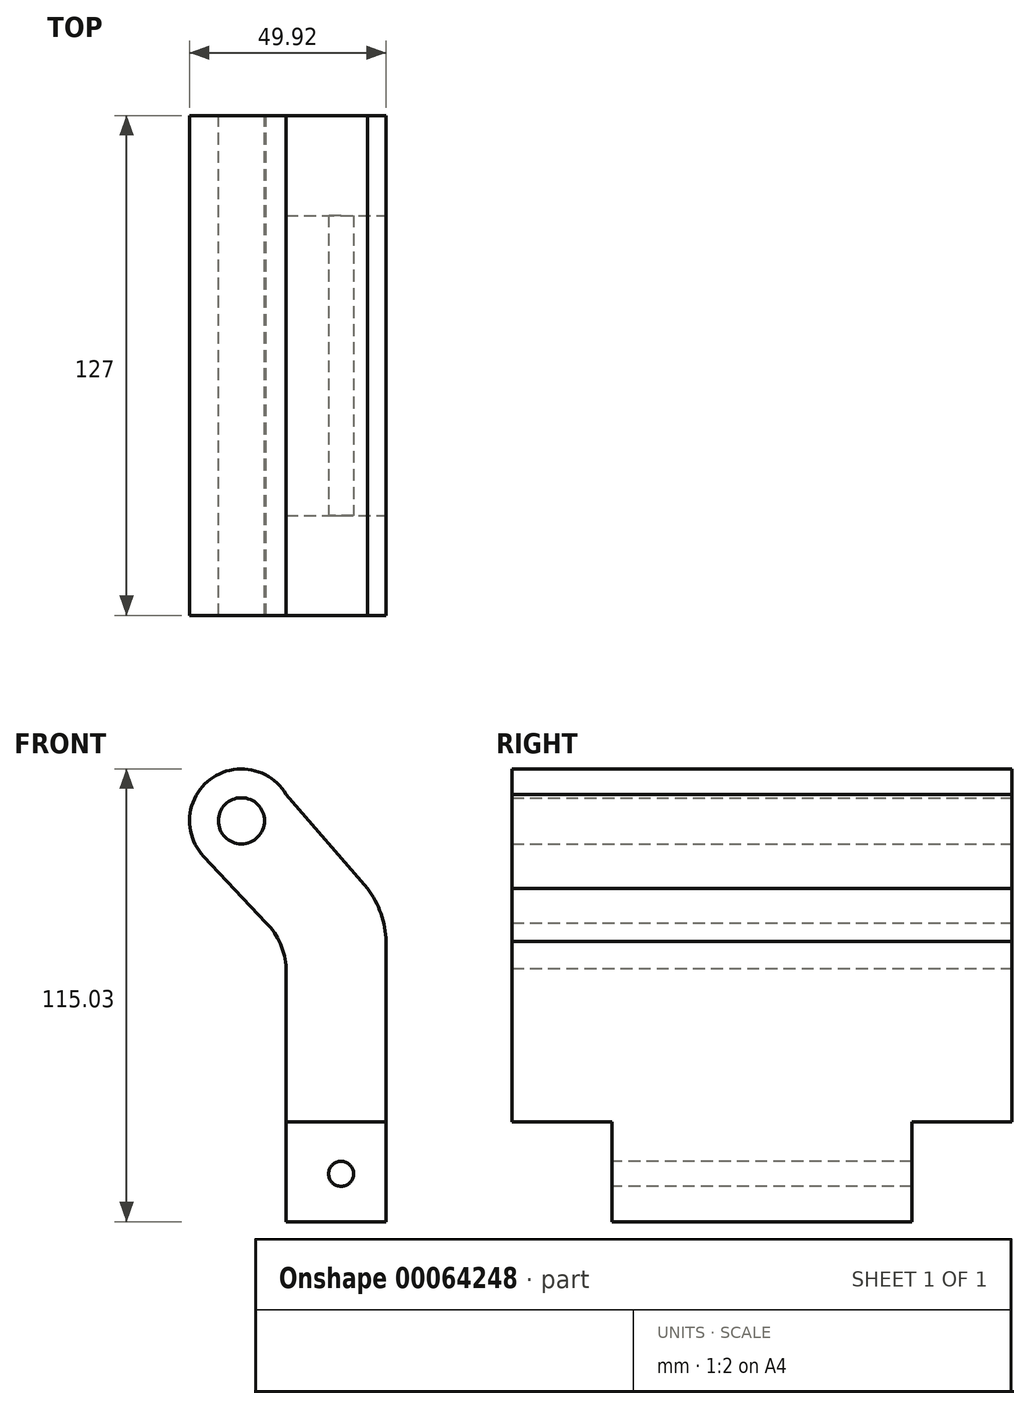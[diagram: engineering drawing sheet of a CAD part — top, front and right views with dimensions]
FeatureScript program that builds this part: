
annotation { "Feature Type Name" : "Feature", "Feature Type Description" : "" }
export const myFeature = defineFeature(function(context is Context, id is Id, definition is map)
    precondition{}
    {
        {
            var Q0;
            Q0=qCreatedBy(makeId("Front.planeOp"),FACE);
            var sketch = newSketch(context, id + "F0", { "sketchPlane" : qUnion([Q0])});
            skLineSegment(sketch, "E0", {"start": v(-13.98, -40.84) * mm, "end": v(11.42, -40.84) * mm});
            skLineSegment(sketch, "E1", {"start": v(-13.98, -40.84) * mm, "end": v(-13.98, 23.48) * mm});
            skLineSegment(sketch, "E2", {"start": v(-18.39, 34.43) * mm, "end": v(-34.91, 51.97) * mm});
            skLineSegment(sketch, "E3", {"start": v(11.42, -40.84) * mm, "end": v(11.42, 30.32) * mm});
            skLineSegment(sketch, "E4", {"start": v(6.68, 43.76) * mm, "end": v(-13.98, 67.73) * mm});
            skArc(sketch, "E5", {"start": v(-13.98, 67.73) * mm, "mid": v(-33.24, 71.54) * mm, "end": v(-34.91, 51.97) * mm});
            skArc(sketch, "E6", {"start": v(-13.98, 23.48) * mm, "mid": v(-15.4, 29.75) * mm, "end": v(-19, 35.08) * mm});
            skArc(sketch, "E7", {"start": v(11.42, 29.42) * mm, "mid": v(10.28, 37) * mm, "end": v(6.68, 43.76) * mm});
            skCircle(sketch, "E8", {"center": v(-25.32, 61) * mm, "radius": 5.86 * mm});
            skSolve(sketch);
        }
        {
            var Q0;
            {var subQ1=sQuery(id+"F0.wireOp",EDGE,"E0");Q0=makeQuery(id+"F0.imprint","IMPRINT",FACE,{"disambiguationData":[TD([[makeQuery(id+"F0.imprint","IMPRINT",EDGE,{"derivedFrom":subQ1}),1.0]])]});}
            extrude(context, id + "F1", {"entities" : qUnion([Q0]), "depth" : 127 * mm});
        }
        {
            var Q0;
            Q0=makeQuery(id+"F1.opExtrude","CAP_FACE",FACE,{"disambiguationData":[OSD([sQuery(id+"F0.wireOp",EDGE,"E0"),sQuery(id+"F0.wireOp",EDGE,"E1"),sQuery(id+"F0.wireOp",EDGE,"E2"),sQuery(id+"F0.wireOp",EDGE,"E3"),sQuery(id+"F0.wireOp",EDGE,"E4"),sQuery(id+"F0.wireOp",EDGE,"E5"),sQuery(id+"F0.wireOp",EDGE,"E6"),sQuery(id+"F0.wireOp",EDGE,"E7")])],"isStart":false});
            var sketch = newSketch(context, id + "F2", { "sketchPlane" : qUnion([Q0])});
            skLineSegment(sketch, "E9", {"start": v(-13.98, -15.44) * mm, "end": v(11.42, -15.44) * mm});
            skLineSegment(sketch, "E10", {"start": v(11.42, -15.44) * mm, "end": v(11.42, -40.84) * mm});
            skLineSegment(sketch, "E11", {"start": v(11.42, -40.84) * mm, "end": v(-13.98, -40.84) * mm});
            skLineSegment(sketch, "E12", {"start": v(-13.98, -40.84) * mm, "end": v(-13.98, -15.44) * mm});
            skSolve(sketch);
        }
        {
            var Q0;
            Q0=makeQuery(id+"F2.imprint","IMPRINT",FACE,{"disambiguationData":[TD([[makeQuery(id+"F2.imprint","IMPRINT",EDGE,{"derivedFrom":sQuery(id+"F2.wireOp",EDGE,"E9")}),-1.0]])]});
            extrude(context, id + "F3", {"entities" : qUnion([Q0]), "operationType" : NewBodyOperationType.REMOVE, "oppositeDirection" : true, "depth" : 25.4 * mm});
        }
        {
            var Q0;
            Q0=makeQuery(id+"F1.opExtrude","CAP_FACE",FACE,{"disambiguationData":[OSD([sQuery(id+"F0.wireOp",EDGE,"E0"),sQuery(id+"F0.wireOp",EDGE,"E1"),sQuery(id+"F0.wireOp",EDGE,"E2"),sQuery(id+"F0.wireOp",EDGE,"E3"),sQuery(id+"F0.wireOp",EDGE,"E4"),sQuery(id+"F0.wireOp",EDGE,"E5"),sQuery(id+"F0.wireOp",EDGE,"E6"),sQuery(id+"F0.wireOp",EDGE,"E7")])],"isStart":true});
            var sketch = newSketch(context, id + "F4", { "sketchPlane" : qUnion([Q0])});
            skLineSegment(sketch, "E13", {"start": v(-11.42, -15.44) * mm, "end": v(13.98, -15.44) * mm});
            skLineSegment(sketch, "E14", {"start": v(13.98, -15.44) * mm, "end": v(13.98, -40.84) * mm});
            skLineSegment(sketch, "E15", {"start": v(13.98, -40.84) * mm, "end": v(-11.42, -40.84) * mm});
            skLineSegment(sketch, "E16", {"start": v(-11.42, -40.84) * mm, "end": v(-11.42, -15.44) * mm});
            skSolve(sketch);
        }
        {
            var Q0;
            Q0=makeQuery(id+"F4.imprint","IMPRINT",FACE,{"disambiguationData":[TD([[makeQuery(id+"F4.imprint","IMPRINT",EDGE,{"derivedFrom":sQuery(id+"F4.wireOp",EDGE,"E13")}),-1.0]])]});
            extrude(context, id + "F5", {"entities" : qUnion([Q0]), "operationType" : NewBodyOperationType.REMOVE, "oppositeDirection" : true, "depth" : 25.4 * mm});
        }
        {
            var Q0;
            Q0=makeQuery(id+"F3.boolean.opBoolean","COPY",FACE,{"derivedFrom":makeQuery(id+"F3.opExtrude","CAP_FACE",FACE,{"disambiguationData":[OSD([sQuery(id+"F2.wireOp",EDGE,"E9"),sQuery(id+"F2.wireOp",EDGE,"E10"),sQuery(id+"F2.wireOp",EDGE,"E11"),sQuery(id+"F2.wireOp",EDGE,"E12")])],"isStart":false})});
            var sketch = newSketch(context, id + "F6", { "sketchPlane" : qUnion([Q0])});
            skCircle(sketch, "E17", {"center": v(0, -28.69) * mm, "radius": 5.4 * mm});
            skSolve(sketch);
        }
        {
            var Q0;
            Q0=sQuery(id+"F6.wireOp",VERTEX,"E17.center");
            var Q1;
            Q1=makeQuery(id+"F1.opExtrude","SWEPT_BODY",BODY,{"disambiguationData":[OSD([sQuery(id+"F0.wireOp",EDGE,"E0"),sQuery(id+"F0.wireOp",EDGE,"E1"),sQuery(id+"F0.wireOp",EDGE,"E2"),sQuery(id+"F0.wireOp",EDGE,"E3"),sQuery(id+"F0.wireOp",EDGE,"E4"),sQuery(id+"F0.wireOp",EDGE,"E5"),sQuery(id+"F0.wireOp",EDGE,"E6"),sQuery(id+"F0.wireOp",EDGE,"E7")])]});
            hole(context, id + "F7", {"style" : HoleStyle.SIMPLE, "holeDiameter" : 6.35 * mm, "endStyle" : HoleEndStyle.THROUGH, "locations" : qUnion([Q0]), "scope" : qUnion([Q1])});
        }
    });
